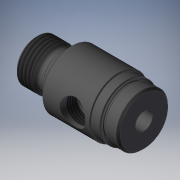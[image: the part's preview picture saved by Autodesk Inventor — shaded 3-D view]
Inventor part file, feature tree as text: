
AUTODESK INVENTOR PART (.ipt)
format: ipt  version: 2019 (Build 230136000, 136)  size: 295,424 bytes
history: native  units: in
note: dims shown in document units (in); Inventor stores cm internally (conversion verified against a paired STEP export)
features: other x119, sketch x6, revolve x5, thread x2, hole x1
ambient origin geometry x8: Origin, YZ Plane, XZ Plane, XY Plane, X Axis, Y Axis, Z Axis, Center Point
bodies: Solid1 (feature_tree)
feature tree (133):
  revolve  "Revolution1"  [1 undecoded]
  thread  "Thread1"  [1 undecoded]
  revolve  "Revolution2"  Angle=360.0deg
  hole  "Hole1"  [1 undecoded]
  revolve  "Revolution3"  [1 undecoded]
  revolve  "Revolution4"  [1 undecoded]
  thread  "Thread2"  [1 undecoded]
  revolve  "Revolution5"  [1 undecoded]
  other  "dp1_XY"
  other  "dp1_YZ"
  other  "dp1_ZX"
  other  "dp1_X"
  other  "dp1_Y"
  other  "dp1_Z"
  other  "dp1_Center"
  other  "dp2_XY"
  other  "dp2_YZ"
  other  "dp2_ZX"
  other  "dp2_X"
  other  "dp2_Y"
  other  "dp2_Z"
  other  "dp2_Center"
  other  "hh_XY"
  other  "hh_YZ"
  other  "hh_ZX"
  other  "hh_X"
  other  "hh_Y"
  other  "hh_Z"
  other  "hh_Center"
  other  "port_XY"
  other  "port_YZ"
  other  "port_ZX"
  other  "port_X"
  other  "port_Y"
  other  "port_Z"
  other  "port_Center"
  other  "rod_guide_XY"
  other  "rod_guide_YZ"
  other  "rod_guide_ZX"
  other  "rod_guide_X"
  other  "rod_guide_Y"
  other  "rod_guide_Z"
  other  "rod_guide_Center"
  other  "s1_XY"
  other  "s1_YZ"
  other  "s1_ZX"
  other  "s1_X"
  other  "s1_Y"
  other  "s1_Z"
  other  "s1_Center"
  other  "s2_XY"
  other  "s2_YZ"
  other  "s2_ZX"
  other  "s2_X"
  other  "s2_Y"
  other  "s2_Z"
  other  "s2_Center"
  other  "t1_XY"
  other  "t1_YZ"
  other  "t1_ZX"
  other  "t1_X"
  other  "t1_Y"
  other  "t1_Z"
  other  "t1_Center"
  other  "t111_XY"
  other  "t111_YZ"
  other  "t111_ZX"
  other  "t111_X"
  other  "t111_Y"
  other  "t111_Z"
  other  "t111_Center"
  other  "to_foot_bracket_XY"
  other  "to_foot_bracket_YZ"
  other  "to_foot_bracket_ZX"
  other  "to_foot_bracket_X"
  other  "to_foot_bracket_Y"
  other  "to_foot_bracket_Z"
  other  "to_foot_bracket_Center"
  other  "to_nut_XY"
  other  "to_nut_YZ"
  other  "to_nut_ZX"
  other  "to_nut_X"
  other  "to_nut_Y"
  other  "to_nut_Z"
  other  "to_nut_Center"
  other  "to_rod_XY"
  other  "to_rod_YZ"
  other  "to_rod_ZX"
  other  "to_rod_X"
  other  "to_rod_Y"
  other  "to_rod_Z"
  other  "to_rod_Center"
  other  "to_screw_XY"
  other  "to_screw_YZ"
  other  "to_screw_ZX"
  other  "to_screw_X"
  other  "to_screw_Y"
  other  "to_screw_Z"
  other  "to_screw_Center"
  other  "to_trunnion_brackets_XY"
  other  "to_trunnion_brackets_YZ"
  other  "to_trunnion_brackets_ZX"
  other  "to_trunnion_brackets_X"
  other  "to_trunnion_brackets_Y"
  other  "to_trunnion_brackets_Z"
  other  "to_trunnion_brackets_Center"
  other  "to_trunnion_brackets1_XY"
  other  "to_trunnion_brackets1_YZ"
  other  "to_trunnion_brackets1_ZX"
  other  "to_trunnion_brackets1_X"
  other  "to_trunnion_brackets1_Y"
  other  "to_trunnion_brackets1_Z"
  other  "to_trunnion_brackets1_Center"
  other  "to_trunnion_brackets2_XY"
  other  "to_trunnion_brackets2_YZ"
  other  "to_trunnion_brackets2_ZX"
  other  "to_trunnion_brackets2_X"
  other  "to_trunnion_brackets2_Y"
  other  "to_trunnion_brackets2_Z"
  other  "to_trunnion_brackets2_Center"
  other  "to_tube_XY"
  other  "to_tube_YZ"
  other  "to_tube_ZX"
  other  "to_tube_X"
  other  "to_tube_Y"
  other  "to_tube_Z"
  other  "to_tube_Center"
  sketch  "Sketch_2"  dims[d0=360.0deg d1=0.23in d2=0.0in d3=360.0deg]
  sketch  "Sketch_3"  dims[d4=0.2535in d5=0.75in d6=0.2735in d7=0.25in d8=90.0deg d9=1.594in d10=0.0in d11=360.0deg]
  sketch  "Sketch3"  dims[d12=360.0deg d13=0.1501in d14=0.0in]
  sketch  "Sketch_10"  dims[d15=360.0deg]
  sketch  "Sketch_40"  dims[d16=0.0in d17=0.0in d18=0.0in d19=0.0in d20=0.0in d21=0.0in]
  sketch  "Sketch_47"
note: 7 required parameter values undecoded (feature->parameter linkage not recoverable at this tier; creation-order binding heuristic only, values carry confidence <= 0.55)